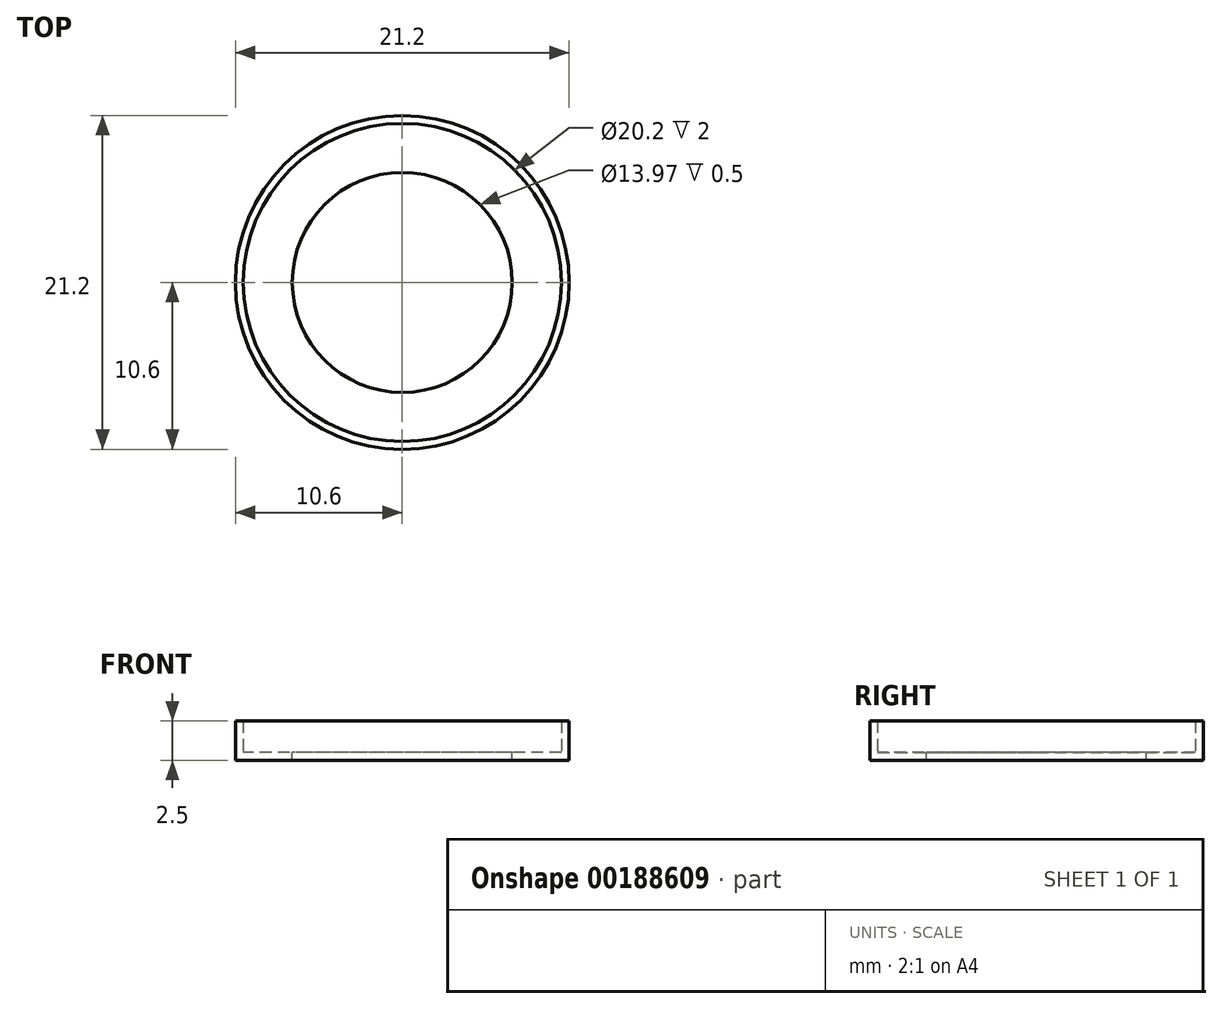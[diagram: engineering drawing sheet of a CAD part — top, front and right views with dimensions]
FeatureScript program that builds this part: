
annotation { "Feature Type Name" : "Feature", "Feature Type Description" : "" }
export const myFeature = defineFeature(function(context is Context, id is Id, definition is map)
    precondition{}
    {
        {
            var Q0;
            Q0=qCreatedBy(makeId("Top.planeOp"),FACE);
            var sketch = newSketch(context, id + "F0", { "sketchPlane" : qUnion([Q0])});
            skCircle(sketch, "E0", {"center": v(0, 0) * mm, "radius": 10.6 * mm});
            skSolve(sketch);
        }
        {
            var Q0;
            Q0 = qSketchRegion(id + "F0", true);
            extrude(context, id + "F1", {"entities" : qUnion([Q0]), "depth" : 1 * mm});
        }
        {
            var Q0;
            Q0=makeQuery(id+"F1.opExtrude","CAP_FACE",FACE,{"disambiguationData":[OSD([sQuery(id+"F0.wireOp",EDGE,"E0")])],"isStart":false});
            shell(context, id + "F2", {"entities" : qUnion([Q0]), "thickness" : .5 * mm});
        }
        {
            var Q0;
            {var subQ0=sQuery(id+"F0.wireOp",EDGE,"E0");Q0=makeQuery(id+"F2.opShell","OFFSET_FACE",FACE,{"disambiguationData":[OSD([subQ0]),TDD([makeQuery(id+"F1.opExtrude","CAP_FACE",FACE,{"disambiguationData":[OSD([subQ0])],"isStart":true})])]});}
            var sketch = newSketch(context, id + "F3", { "sketchPlane" : qUnion([Q0])});
            skCircle(sketch, "E1", {"center": v(0, 0) * mm, "radius": 6.99 * mm});
            skSolve(sketch);
        }
        {
            var Q0;
            Q0 = qSketchRegion(id + "F3", true);
            extrude(context, id + "F4", {"entities" : qUnion([Q0]), "operationType" : NewBodyOperationType.REMOVE, "oppositeDirection" : true, "depth" : 25 * mm});
        }
        {
            var Q0;
            Q0=makeQuery(id+"F1.opExtrude","CAP_FACE",FACE,{"disambiguationData":[OSD([sQuery(id+"F0.wireOp",EDGE,"E0")])],"isStart":false});
            var sketch = newSketch(context, id + "F5", { "sketchPlane" : qUnion([Q0])});
            skCircle(sketch, "E2.0", {"center": v(0, 0) * mm, "radius": 10.6 * mm});
            skCircle(sketch, "E3.0", {"center": v(0, 0) * mm, "radius": 10.1 * mm});
            skSolve(sketch);
        }
        {
            var Q0;
            Q0 = qSketchRegion(id + "F5", true);
            extrude(context, id + "F6", {"entities" : qUnion([Q0]), "operationType" : NewBodyOperationType.ADD, "depth" : 1.5 * mm});
        }
    });
